FCSTD DOCUMENT  (FreeCAD 0.20R)
Label: outer_plate
License: All rights reserved
LicenseURL: http://en.wikipedia.org/wiki/All_rights_reserved
objects: Sketcher::SketchObject×1, PartDesign::Body×1
note: 2 computed .brp shape members not serialized (recipe doc carries the construction recipe); baked Part::Feature solids carry a one-line shape summary decoded from their .brp

FEATURE [Sketcher::SketchObject] Sketch
  FullyConstrained = false
  MapMode = 5
  Support = -> [XY_Plane]
  sketch-geometry (44):
    g0: LineSegment StartX=0.5 StartY=-0.136146 StartZ=0 EndX=285.241 EndY=-0.136146 EndZ=0
    g1: LineSegment StartX=285.741 StartY=-0.636146 StartZ=0 EndX=285.741 EndY=-94.8861 EndZ=0
    g2: LineSegment StartX=285.241 StartY=-95.3861 StartZ=0 EndX=0.5 EndY=-95.3861 EndZ=0
    g3: LineSegment StartX=0 StartY=-94.8861 StartZ=0 EndX=0 EndY=-0.636146 EndZ=0
    g4: LineSegment StartX=0.5 StartY=23.6769 StartZ=0 EndX=18.55 EndY=23.6769 EndZ=0
    g5: LineSegment StartX=19.05 StartY=23.1769 StartZ=0 EndX=19.05 EndY=5.12685 EndZ=0
    g6: LineSegment StartX=18.55 StartY=4.62685 StartZ=0 EndX=0.5 EndY=4.62685 EndZ=0
    g7: LineSegment StartX=0 StartY=5.12685 StartZ=0 EndX=0 EndY=23.1769 EndZ=0
    g8: LineSegment StartX=38.6 StartY=23.6769 StartZ=0 EndX=113.8 EndY=23.6769 EndZ=0
    g9: LineSegment StartX=114.3 StartY=23.1769 StartZ=0 EndX=114.3 EndY=5.12685 EndZ=0
    g10: LineSegment StartX=113.8 StartY=4.62685 StartZ=0 EndX=38.6 EndY=4.62685 EndZ=0
    g11: LineSegment StartX=38.1 StartY=5.12685 StartZ=0 EndX=38.1 EndY=23.1769 EndZ=0
    g12: ArcOfCircle CenterX=124.325 CenterY=23.1769 CenterZ=0 NormalX=0 NormalY=0 NormalZ=1 AngleXU=0 Radius=0.5 StartAngle=1.5708 EndAngle=3.14159
    g13: LineSegment StartX=124.325 StartY=23.6769 StartZ=0 EndX=199.525 EndY=23.6769 EndZ=0
    g14: ArcOfCircle CenterX=199.525 CenterY=23.1769 CenterZ=0 NormalX=0 NormalY=0 NormalZ=1 AngleXU=0 Radius=0.5 StartAngle=-2.7e-15 EndAngle=1.5708
    g15: LineSegment StartX=200.025 StartY=23.1769 StartZ=0 EndX=200.025 EndY=5.12685 EndZ=0
    g16: ArcOfCircle CenterX=199.525 CenterY=5.12685 CenterZ=0 NormalX=0 NormalY=0 NormalZ=1 AngleXU=0 Radius=0.5 StartAngle=4.71239 EndAngle=6.28319
    g17: LineSegment StartX=199.525 StartY=4.62685 StartZ=0 EndX=124.325 EndY=4.62685 EndZ=0
    g18: ArcOfCircle CenterX=124.325 CenterY=5.12685 CenterZ=0 NormalX=0 NormalY=0 NormalZ=1 AngleXU=0 Radius=0.5 StartAngle=3.14159 EndAngle=4.71239
    g19: LineSegment StartX=123.825 StartY=5.12685 StartZ=0 EndX=123.825 EndY=23.1769 EndZ=0
    g20: GeomPoint X=123.825 Y=23.6769 Z=0
    g21: GeomPoint X=200.025 Y=4.62685 Z=0
    g22: ArcOfCircle CenterX=285.241 CenterY=-0.636146 CenterZ=0 NormalX=0 NormalY=0 NormalZ=1 AngleXU=0 Radius=0.5 StartAngle=0 EndAngle=1.5708
    g23: ArcOfCircle CenterX=0.5 CenterY=-0.636146 CenterZ=0 NormalX=0 NormalY=0 NormalZ=1 AngleXU=0 Radius=0.5 StartAngle=1.5708 EndAngle=3.14159
    g24: ArcOfCircle CenterX=0.5 CenterY=-94.8861 CenterZ=0 NormalX=0 NormalY=0 NormalZ=1 AngleXU=0 Radius=0.5 StartAngle=3.14159 EndAngle=4.71239
    g25: ArcOfCircle CenterX=285.241 CenterY=-94.8861 CenterZ=0 NormalX=0 NormalY=0 NormalZ=1 AngleXU=0 Radius=0.5 StartAngle=4.71239 EndAngle=6.28319
    g26: ArcOfCircle CenterX=0.5 CenterY=23.1769 CenterZ=0 NormalX=0 NormalY=0 NormalZ=1 AngleXU=0 Radius=0.5 StartAngle=1.5708 EndAngle=3.14159
    g27: ArcOfCircle CenterX=0.5 CenterY=5.12685 CenterZ=0 NormalX=0 NormalY=0 NormalZ=1 AngleXU=0 Radius=0.5 StartAngle=3.14159 EndAngle=4.71239
    g28: ArcOfCircle CenterX=18.55 CenterY=5.12685 CenterZ=0 NormalX=0 NormalY=0 NormalZ=1 AngleXU=0 Radius=0.5 StartAngle=4.71239 EndAngle=6.28319
    g29: ArcOfCircle CenterX=18.55 CenterY=23.1769 CenterZ=0 NormalX=0 NormalY=0 NormalZ=1 AngleXU=0 Radius=0.5 StartAngle=1.7e-15 EndAngle=1.5708
    g30: ArcOfCircle CenterX=38.6 CenterY=23.1769 CenterZ=0 NormalX=0 NormalY=0 NormalZ=1 AngleXU=0 Radius=0.5 StartAngle=1.5708 EndAngle=3.14159
    g31: ArcOfCircle CenterX=38.6 CenterY=5.12685 CenterZ=0 NormalX=0 NormalY=0 NormalZ=1 AngleXU=0 Radius=0.5 StartAngle=3.14159 EndAngle=4.71239
    g32: ArcOfCircle CenterX=113.8 CenterY=5.12685 CenterZ=0 NormalX=0 NormalY=0 NormalZ=1 AngleXU=0 Radius=0.5 StartAngle=4.71239 EndAngle=6.28319
    g33: ArcOfCircle CenterX=113.8 CenterY=23.1769 CenterZ=0 NormalX=0 NormalY=0 NormalZ=1 AngleXU=0 Radius=0.5 StartAngle=3e-16 EndAngle=1.5708
    g34: ArcOfCircle CenterX=210.05 CenterY=23.1769 CenterZ=0 NormalX=0 NormalY=0 NormalZ=1 AngleXU=0 Radius=0.5 StartAngle=1.5708 EndAngle=3.14159
    g35: LineSegment StartX=210.05 StartY=23.6769 StartZ=0 EndX=285.25 EndY=23.6769 EndZ=0
    g36: ArcOfCircle CenterX=285.25 CenterY=23.1769 CenterZ=0 NormalX=0 NormalY=0 NormalZ=1 AngleXU=0 Radius=0.5 StartAngle=-1.8e-15 EndAngle=1.5708
    g37: LineSegment StartX=285.75 StartY=23.1769 StartZ=0 EndX=285.75 EndY=5.12685 EndZ=0
    g38: ArcOfCircle CenterX=285.25 CenterY=5.12685 CenterZ=0 NormalX=0 NormalY=0 NormalZ=1 AngleXU=0 Radius=0.5 StartAngle=4.71239 EndAngle=6.28319
    g39: LineSegment StartX=285.25 StartY=4.62685 StartZ=0 EndX=210.05 EndY=4.62685 EndZ=0
    g40: ArcOfCircle CenterX=210.05 CenterY=5.12685 CenterZ=0 NormalX=0 NormalY=0 NormalZ=1 AngleXU=0 Radius=0.5 StartAngle=3.14159 EndAngle=4.71239
    g41: LineSegment StartX=209.55 StartY=5.12685 StartZ=0 EndX=209.55 EndY=23.1769 EndZ=0
    g42: GeomPoint X=209.55 Y=23.6769 Z=0
    g43: GeomPoint X=285.75 Y=4.62685 Z=0
  constraints (107):
    c: Horizontal(g0)
    c: Horizontal(g2)
    c: Vertical(g1)
    c: Horizontal(g4)
    c: Horizontal(g6)
    c: Vertical(g5)
    c: Vertical(g7)
    c: Equal(g4,g5)
    c: Horizontal(g8)
    c: Horizontal(g10)
    c: Vertical(g9)
    c: Vertical(g11)
    c: Equal(g11,g5)
    c: Tangent(g12,g13) = 1.5708
    c: Tangent(g13,g14) = 1.5708
    c: Tangent(g14,g15) = 1.5708
    c: Tangent(g15,g16) = 1.5708
    c: Tangent(g16,g17) = 1.5708
    c: Tangent(g17,g18) = 1.5708
    c: Tangent(g18,g19) = 1.5708
    c: Tangent(g19,g12) = 1.5708
    c: Horizontal(g13)
    c: Horizontal(g17)
    c: Vertical(g15)
    c: Vertical(g19)
    c: Equal(g12,g14)
    c: Equal(g14,g16)
    c: Equal(g16,g18)
    c: PointOnObject(g20,g13)
    c: PointOnObject(g20,g19)
    c: PointOnObject(g21,g15)
    c: PointOnObject(g21,g17)
    c: Tangent(g0,g22) = 1.5708
    c: Tangent(g1,g22) = 1.5708
    c: Tangent(g0,g23) = 1.5708
    c: Tangent(g3,g23) = 1.5708
    c: Tangent(g2,g24) = 1.5708
    c: Tangent(g3,g24) = 1.5708
    c: Tangent(g1,g25) = 1.5708
    c: Tangent(g2,g25) = 1.5708
    c: Tangent(g4,g26) = 1.5708
    c: Tangent(g7,g26) = 1.5708
    c: Tangent(g6,g27) = 1.5708
    c: Tangent(g7,g27) = 1.5708
    c: Tangent(g6,g28) = 1.5708
    c: Tangent(g5,g28) = 1.5708
    c: Tangent(g4,g29) = 1.5708
    c: Tangent(g5,g29) = 1.5708
    c: Tangent(g11,g30) = 1.5708
    c: Tangent(g8,g30) = 1.5708
    c: Tangent(g10,g31) = 1.5708
    c: Tangent(g11,g31) = 1.5708
    c: Tangent(g10,g32) = 1.5708
    c: Tangent(g9,g32) = 1.5708
    c: Tangent(g8,g33) = 1.5708
    c: Tangent(g9,g33) = 1.5708
    c: Radius(g23) = 0.5
    c: Tangent(g-2,g3)
    c: Equal(g23,g24)
    c: Equal(g24,g25)
    c: Equal(g25,g22)
    c: Equal(g23,g27)
    c: Equal(g27,g26)
    c: Equal(g29,g26)
    c: Equal(g26,g28)
    c: Equal(g28,g31)
    c: Equal(g31,g30)
    c: Equal(g30,g33)
    c: Equal(g33,g32)
    c: Equal(g32,g18)
    c: Tangent(g3,g-2)
    c: Vertical(g3,g7)
    c: Horizontal(g6,g10)
    c: Horizontal(g10,g17)
    c: Horizontal(g8,g12)
    c: DistanceX(g5,g11) = 19.05
    c: DistanceY(g0,g6) = 4.763
    c: DistanceX(g11,g9) = 76.2
    c: DistanceX(g9,g18) = 9.525
    c: Equal(g10,g17)
    c: DistanceX(g3,g1) = 285.741
    c: DistanceY(g2,g0) = 95.25
    c: Tangent(g34,g35) = 1.5708
    c: Tangent(g35,g36) = 1.5708
    c: Tangent(g36,g37) = 1.5708
    c: Tangent(g37,g38) = 1.5708
    c: Tangent(g38,g39) = 1.5708
    c: Tangent(g39,g40) = 1.5708
    c: Tangent(g40,g41) = 1.5708
    c: Tangent(g41,g34) = 1.5708
    c: Horizontal(g35)
    c: Horizontal(g39)
    c: Vertical(g37)
    c: Vertical(g41)
    c: Equal(g34,g36)
    c: Equal(g36,g38)
    c: Equal(g38,g40)
    c: PointOnObject(g42,g35)
    c: PointOnObject(g42,g41)
    c: PointOnObject(g43,g37)
    c: PointOnObject(g43,g39)
    c: Equal(g34,g14)
    c: Equal(g35,g13)
    c: Equal(g41,g15)
    c: Horizontal(g39,g16)
    c: DistanceX(g15,g40) = 9.525
    c: DistanceY(g6,g4) = 19.05
FEATURE [PartDesign::Body] Body
  Group = -> [Sketch]
  Origin = -> Origin
